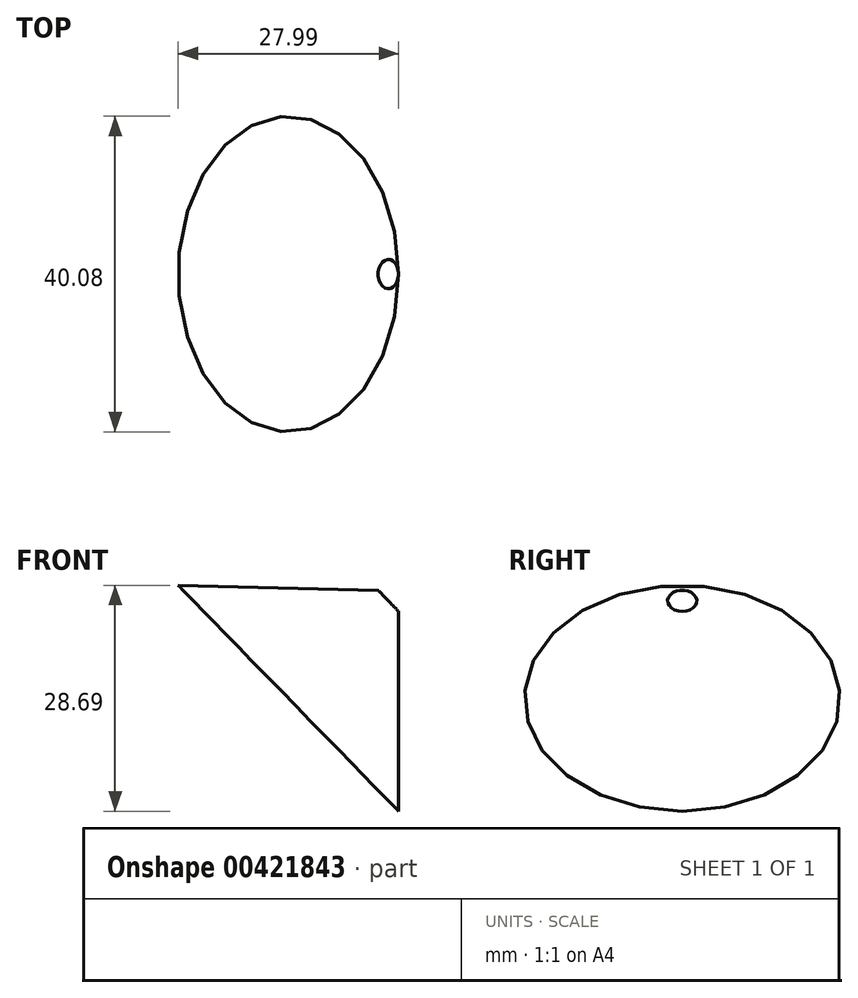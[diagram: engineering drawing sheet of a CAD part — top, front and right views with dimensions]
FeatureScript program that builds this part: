
annotation { "Feature Type Name" : "Feature", "Feature Type Description" : "" }
export const myFeature = defineFeature(function(context is Context, id is Id, definition is map)
    precondition{}
    {
        {
            var Q0;
            Q0=qCreatedBy(makeId("Front.planeOp"),FACE);
            var sketch = newSketch(context, id + "F0", { "sketchPlane" : qUnion([Q0])});
            skLineSegment(sketch, "E0", {"start": v(0, 0) * mm, "end": v(54.54, 53.21) * mm});
            skLineSegment(sketch, "E1", {"start": v(0, 0) * mm, "end": v(0, -25.4) * mm});
            skLineSegment(sketch, "E2", {"start": v(0, -25.4) * mm, "end": v(-12.7, -25.4) * mm});
            skLineSegment(sketch, "E3", {"start": v(-12.7, 2.6) * mm, "end": v(-12.7, -25.4) * mm});
            skLineSegment(sketch, "E4", {"start": v(-12.7, 2.6) * mm, "end": v(0, 2.6) * mm});
            skLineSegment(sketch, "E5", {"start": v(0, 2.6) * mm, "end": v(53.11, 54.4) * mm});
            skSolve(sketch);
        }
        {
            var Q0;
            Q0=sQuery(id+"F0.wireOp",EDGE,"E1");
            var Q1;
            Q1=sQuery(id+"F0.wireOp",EDGE,"E5");
            revolve(context, id + "F1", {"bodyType" : ToolBodyType.SURFACE, "surfaceEntities" : qUnion([Q0]), "axis" : qUnion([Q1]), "revolveType" : RevolveType.FULL});
        }
    });
